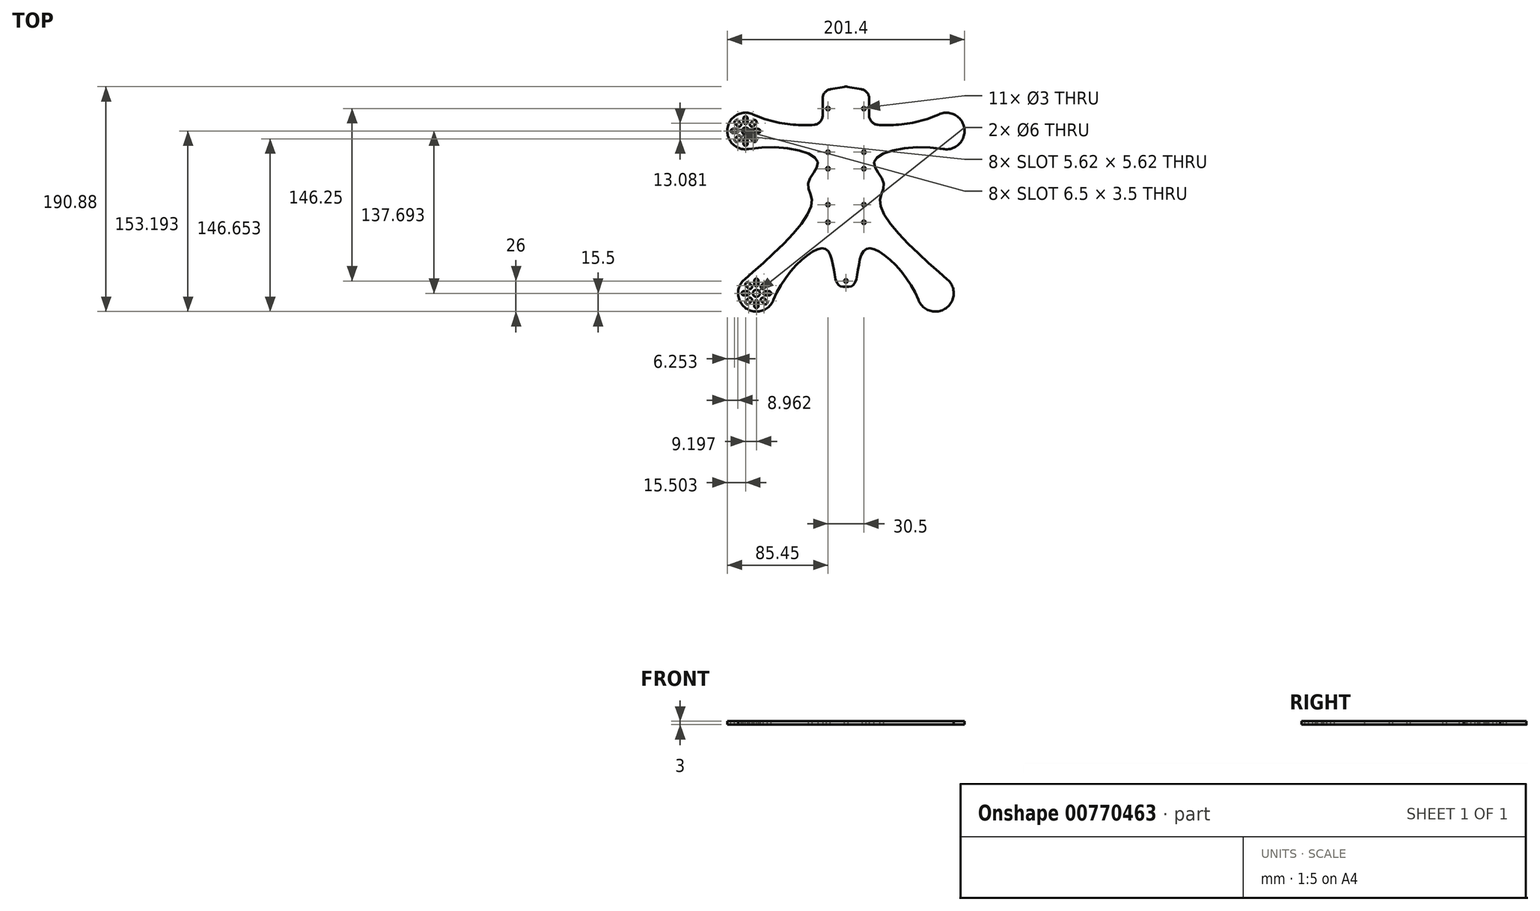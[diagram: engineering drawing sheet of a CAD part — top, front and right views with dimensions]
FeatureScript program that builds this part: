
annotation { "Feature Type Name" : "Feature", "Feature Type Description" : "" }
export const myFeature = defineFeature(function(context is Context, id is Id, definition is map)
    precondition{}
    {
        {
            var Q0;
            Q0=qCreatedBy(makeId("Top.planeOp"),FACE);
            var sketch = newSketch(context, id + "F0", { "sketchPlane" : qUnion([Q0])});
            skCircle(sketch, "E0", {"center": v(76, -77.5) * mm, "radius": 63.5 * mm, "construction": true});
            skLineSegment(sketch, "E1", {"start": v(0, 110) * mm, "end": v(0, -110) * mm, "construction": true});
            skLineSegment(sketch, "E2", {"start": v(-112.76, 0) * mm, "end": v(107.24, 0) * mm, "construction": true});
            skCircle(sketch, "E3", {"center": v(-85.2, 60.2) * mm, "radius": 63.5 * mm, "construction": true});
            skCircle(sketch, "E4", {"center": v(-76, -77.5) * mm, "radius": 63.5 * mm, "construction": true});
            skCircle(sketch, "E5", {"center": v(85.2, 60.2) * mm, "radius": 63.5 * mm, "construction": true});
            skLineSegment(sketch, "E6", {"start": v(-85.2, 60.2) * mm, "end": v(76, -77.5) * mm, "construction": true});
            skLineSegment(sketch, "E7", {"start": v(85.2, 60.2) * mm, "end": v(-76, -77.5) * mm, "construction": true});
            skLineSegment(sketch, "E8", {"start": v(-85.2, 60.2) * mm, "end": v(85.2, 60.2) * mm, "construction": true});
            skLineSegment(sketch, "E9", {"start": v(-76, -77.5) * mm, "end": v(76, -77.5) * mm, "construction": true});
            skLineSegment(sketch, "E10", {"start": v(85.2, 60.2) * mm, "end": v(76, -77.5) * mm, "construction": true});
            skLineSegment(sketch, "E11", {"start": v(-85.2, 60.2) * mm, "end": v(-76, -77.5) * mm, "construction": true});
            skCircle(sketch, "E12", {"center": v(76, -77.5) * mm, "radius": 11.5 * mm, "construction": true});
            skArc(sketch, "E13", {"start": v(61.56, -83.13) * mm, "mid": v(84.93, -90.17) * mm, "end": v(86.16, -65.8) * mm});
            skArc(sketch, "E14", {"start": v(82.42, 44.94) * mm, "mid": v(100.57, 62.2) * mm, "end": v(78.61, 74.23) * mm});
            skLineSegment(sketch, "E15", {"start": v(0, 98) * mm, "end": v(0, -72) * mm, "construction": true});
            skFitSpline(sketch, "E16", {"points": [v(82.42, 44.94) * mm, v(24, 34.2) * mm, v(32, 16.2) * mm, v(29, -2) * mm, v(86.16, -65.8) * mm], "startDerivative": vector(-245.99, 44.84) * mm, "endDerivative": vector(157.3, -136.44) * mm});
            skLineSegment(sketch, "E17", {"start": v(86.16, -65.8) * mm, "end": v(67.27, -49.4) * mm, "construction": true});
            skLineSegment(sketch, "E18", {"start": v(82.42, 44.94) * mm, "end": v(57.82, 49.43) * mm, "construction": true});
            skLineSegment(sketch, "E19.bottom", {"start": v(15.25, 28.25) * mm, "end": v(-15.25, 28.25) * mm, "construction": true});
            skLineSegment(sketch, "E19.top", {"start": v(15.25, -2.25) * mm, "end": v(-15.25, -2.25) * mm, "construction": true});
            skLineSegment(sketch, "E19.left", {"start": v(15.25, 28.25) * mm, "end": v(15.25, -2.25) * mm, "construction": true});
            skLineSegment(sketch, "E19.right", {"start": v(-15.25, 28.25) * mm, "end": v(-15.25, -2.25) * mm, "construction": true});
            skPoint(sketch, "E19.middle", {"position": v(0, 13) * mm});
            skCircle(sketch, "E20", {"center": v(15.25, 28.25) * mm, "radius": 1.5 * mm});
            skCircle(sketch, "E21", {"center": v(-15.25, 28.25) * mm, "radius": 1.5 * mm});
            skCircle(sketch, "E22", {"center": v(-15.25, -2.25) * mm, "radius": 1.5 * mm});
            skCircle(sketch, "E23", {"center": v(15.25, -2.25) * mm, "radius": 1.5 * mm});
            skLineSegment(sketch, "E24.bottom", {"start": v(18, 31) * mm, "end": v(-18, 31) * mm, "construction": true});
            skLineSegment(sketch, "E24.top", {"start": v(18, -5) * mm, "end": v(-18, -5) * mm, "construction": true});
            skLineSegment(sketch, "E24.left", {"start": v(18, 31) * mm, "end": v(18, -5) * mm, "construction": true});
            skLineSegment(sketch, "E24.right", {"start": v(-18, 31) * mm, "end": v(-18, -5) * mm, "construction": true});
            skCircle(sketch, "E25", {"center": v(15.25, 42.25) * mm, "radius": 1.5 * mm});
            skCircle(sketch, "E26", {"center": v(15.25, 79.25) * mm, "radius": 1.5 * mm});
            skCircle(sketch, "E27", {"center": v(15.25, -17.25) * mm, "radius": 1.5 * mm});
            skCircle(sketch, "E28", {"center": v(0, -67) * mm, "radius": 1.5 * mm});
            skFitSpline(sketch, "E29", {"points": [v(61.56, -83.13) * mm, v(17, -40) * mm, v(8, -68) * mm, v(0, -72) * mm], "startDerivative": vector(-56.32, 144.55) * mm, "endDerivative": vector(-62, 0) * mm});
            skLineSegment(sketch, "E30", {"start": v(0, -72) * mm, "end": v(3.8, -72) * mm});
            skLineSegment(sketch, "E31", {"start": v(61.56, -83.13) * mm, "end": v(52.48, -59.83) * mm, "construction": true});
            skFitSpline(sketch, "E32.MirrorCS", {"points": [v(-61.56, -83.13) * mm, v(-17, -40) * mm, v(-8, -68) * mm, v(0, -72) * mm], "startDerivative": vector(56.32, 144.55) * mm, "endDerivative": vector(62, 0) * mm});
            skArc(sketch, "E33.MirrorC", {"start": v(-61.56, -83.13) * mm, "mid": v(-84.93, -90.17) * mm, "end": v(-86.16, -65.8) * mm});
            skFitSpline(sketch, "E34.MirrorCS", {"points": [v(-82.42, 44.94) * mm, v(-24, 34.2) * mm, v(-32, 16.2) * mm, v(-29, -2) * mm, v(-86.16, -65.8) * mm], "startDerivative": vector(245.99, 44.84) * mm, "endDerivative": vector(-157.3, -136.44) * mm});
            skArc(sketch, "E35.MirrorC", {"start": v(-82.42, 44.94) * mm, "mid": v(-100.57, 62.2) * mm, "end": v(-78.61, 74.23) * mm});
            skLineSegment(sketch, "E36", {"start": v(15.25, -17.25) * mm, "end": v(15.25, 79.25) * mm, "construction": true});
            skCircle(sketch, "E37.MirrorC", {"center": v(-15.25, 79.25) * mm, "radius": 1.5 * mm});
            skCircle(sketch, "E38.MirrorC", {"center": v(-15.25, 42.25) * mm, "radius": 1.5 * mm});
            skCircle(sketch, "E39.MirrorC", {"center": v(-15.25, -17.25) * mm, "radius": 1.5 * mm});
            skLineSegment(sketch, "E40", {"start": v(0, 98) * mm, "end": v(19.7, 94.53) * mm});
            skLineSegment(sketch, "E41", {"start": v(19.7, 94.53) * mm, "end": v(19.7, 66.53) * mm});
            skFitSpline(sketch, "E42", {"points": [v(19.7, 66.53) * mm, v(78.61, 74.23) * mm], "startDerivative": vector(29.71, -6.37) * mm, "endDerivative": vector(67.9, 31.86) * mm});
            skLineSegment(sketch, "E43", {"start": v(78.61, 74.23) * mm, "end": v(55.98, 63.6) * mm, "construction": true});
            skLineSegment(sketch, "E44.MirrorCS", {"start": v(0, 98) * mm, "end": v(-19.7, 94.53) * mm});
            skLineSegment(sketch, "E45.MirrorCS", {"start": v(-19.7, 94.53) * mm, "end": v(-19.7, 66.53) * mm});
            skFitSpline(sketch, "E46.MirrorCS", {"points": [v(-19.7, 66.53) * mm, v(-78.61, 74.23) * mm], "startDerivative": vector(-29.71, -6.37) * mm, "endDerivative": vector(-67.9, 31.86) * mm});
            skSolve(sketch);
        }
        {
            var Q0;
            {var subQ0=sQuery(id+"F0.wireOp",EDGE,"E35.MirrorC");var subQ1=makeQuery(id+"F0.imprint","INTERSECT",VERTEX,{"derivedFrom":[sQuery(id+"F0.wireOp",EDGE,"E34.MirrorCS"),subQ0]});Q0=makeQuery(id+"F0.imprint","IMPRINT",FACE,{"disambiguationData":[TD([[makeQuery(id+"F0.imprint","IMPRINT",EDGE,{"disambiguationData":[TD([[subQ1,1.0]])],"derivedFrom":subQ0}),-1.0]])]});}
            var Q1;
            Q1=makeQuery(id+"F0.imprint","IMPRINT",FACE,{"disambiguationData":[TD([[makeQuery(id+"F0.imprint","IMPRINT",EDGE,{"derivedFrom":sQuery(id+"F0.wireOp",EDGE,"E21")}),-1.0]])]});
            var Q2;
            {var subQ6=sQuery(id+"F0.wireOp",EDGE,"eeeb82b9-f415-4523-90a6-ce32b2bf8115");Q2=makeQuery(id+"F0.imprint","IMPRINT",FACE,{"disambiguationData":[TD([[makeQuery(id+"F0.imprint","IMPRINT",EDGE,{"derivedFrom":subQ6}),1.0]])]});}
            var Q3;
            {var subQ0=sQuery(id+"F0.wireOp",EDGE,"E13");var subQ1=makeQuery(id+"F0.imprint","INTERSECT",VERTEX,{"derivedFrom":[subQ0,sQuery(id+"F0.wireOp",EDGE,"E16")]});Q3=makeQuery(id+"F0.imprint","IMPRINT",FACE,{"disambiguationData":[TD([[makeQuery(id+"F0.imprint","IMPRINT",EDGE,{"disambiguationData":[TD([[subQ1,-1.0]])],"derivedFrom":subQ0}),1.0]])]});}
            var Q4;
            {var subQ0=sQuery(id+"F0.wireOp",EDGE,"E33.MirrorC");var subQ1=makeQuery(id+"F0.imprint","INTERSECT",VERTEX,{"derivedFrom":[sQuery(id+"F0.wireOp",EDGE,"E32.MirrorCS"),subQ0]});Q4=makeQuery(id+"F0.imprint","IMPRINT",FACE,{"disambiguationData":[TD([[makeQuery(id+"F0.imprint","IMPRINT",EDGE,{"disambiguationData":[TD([[subQ1,1.0]])],"derivedFrom":subQ0}),-1.0]])]});}
            var Q5;
            {var subQ0=sQuery(id+"F0.wireOp",EDGE,"E14");var subQ1=makeQuery(id+"F0.imprint","INTERSECT",VERTEX,{"derivedFrom":[subQ0,sQuery(id+"F0.wireOp",EDGE,"eeeb82b9-f415-4523-90a6-ce32b2bf8115")]});Q5=makeQuery(id+"F0.imprint","IMPRINT",FACE,{"disambiguationData":[TD([[makeQuery(id+"F0.imprint","IMPRINT",EDGE,{"disambiguationData":[TD([[subQ1,-1.0]])],"derivedFrom":subQ0}),1.0]])]});}
            var Q6;
            {var subQ0=sQuery(id+"F0.wireOp",EDGE,"E16");Q6=makeQuery(id+"F0.imprint","IMPRINT",FACE,{"disambiguationData":[TD([[makeQuery(id+"F0.imprint","IMPRINT",EDGE,{"derivedFrom":subQ0}),-1.0]])]});}
            extrude(context, id + "F1", {"entities" : qUnion([Q0, Q1, Q2, Q3, Q4, Q5, Q6]), "depth" : 3 * mm, "offsetDistance" : 25 * mm});
        }
        {
            var Q0;
            Q0=makeQuery(id+"F1.opExtrude","SWEPT_EDGE",EDGE,{"disambiguationData":[OSD([sQuery(id+"F0.wireOp",EDGE,"E45.MirrorCS"),sQuery(id+"F0.wireOp",EDGE,"E46.MirrorCS")])]});
            var Q1;
            Q1=makeQuery(id+"F1.opExtrude","SWEPT_EDGE",EDGE,{"disambiguationData":[OSD([sQuery(id+"F0.wireOp",EDGE,"E44.MirrorCS"),sQuery(id+"F0.wireOp",EDGE,"E45.MirrorCS")])]});
            var Q2;
            Q2=makeQuery(id+"F1.opExtrude","SWEPT_EDGE",EDGE,{"disambiguationData":[OSD([sQuery(id+"F0.wireOp",EDGE,"E41"),sQuery(id+"F0.wireOp",EDGE,"E42")])]});
            var Q3;
            Q3=makeQuery(id+"F1.opExtrude","SWEPT_EDGE",EDGE,{"disambiguationData":[OSD([sQuery(id+"F0.wireOp",EDGE,"E40"),sQuery(id+"F0.wireOp",EDGE,"E41")])]});
            var Q4;
            Q4=makeQuery(id+"F1.opExtrude","SWEPT_EDGE",EDGE,{"disambiguationData":[OSD([sQuery(id+"F0.wireOp",EDGE,"E40"),sQuery(id+"F0.wireOp",EDGE,"E44.MirrorCS")])]});
            fillet(context, id + "F2", {"entities" : qUnion([Q0, Q1, Q2, Q3, Q4]), "tangentPropagation" : true, "radius" : 8 * mm, "defaultsChanged" : false, "vertexSettings" : [], "allowEdgeOverflow" : false});
        }
        {
            var Q0;
            Q0=makeQuery(id+"F1.opExtrude","CAP_FACE",FACE,{"disambiguationData":[OSD([sQuery(id+"F0.wireOp",EDGE,"E13"),sQuery(id+"F0.wireOp",EDGE,"E14"),sQuery(id+"F0.wireOp",EDGE,"E16"),sQuery(id+"F0.wireOp",EDGE,"E20"),sQuery(id+"F0.wireOp",EDGE,"E21"),sQuery(id+"F0.wireOp",EDGE,"E22"),sQuery(id+"F0.wireOp",EDGE,"E23"),sQuery(id+"F0.wireOp",EDGE,"E25"),sQuery(id+"F0.wireOp",EDGE,"E26"),sQuery(id+"F0.wireOp",EDGE,"E27"),sQuery(id+"F0.wireOp",EDGE,"E28"),sQuery(id+"F0.wireOp",EDGE,"E29"),sQuery(id+"F0.wireOp",EDGE,"E32.MirrorCS"),sQuery(id+"F0.wireOp",EDGE,"E33.MirrorC"),sQuery(id+"F0.wireOp",EDGE,"E34.MirrorCS"),sQuery(id+"F0.wireOp",EDGE,"E35.MirrorC"),sQuery(id+"F0.wireOp",EDGE,"E37.MirrorC"),sQuery(id+"F0.wireOp",EDGE,"E38.MirrorC"),sQuery(id+"F0.wireOp",EDGE,"E39.MirrorC"),sQuery(id+"F0.wireOp",EDGE,"E40"),sQuery(id+"F0.wireOp",EDGE,"E41"),sQuery(id+"F0.wireOp",EDGE,"E42"),sQuery(id+"F0.wireOp",EDGE,"E44.MirrorCS"),sQuery(id+"F0.wireOp",EDGE,"E45.MirrorCS"),sQuery(id+"F0.wireOp",EDGE,"E46.MirrorCS")])],"isStart":false});
            var sketch = newSketch(context, id + "F3", { "sketchPlane" : qUnion([Q0])});
            skArc(sketch, "E47.0", {"start": v(-82.42, 44.94) * mm, "mid": v(-100.57, 62.2) * mm, "end": v(-78.61, 74.23) * mm, "construction": true});
            skArc(sketch, "E47.1", {"start": v(82.42, 44.94) * mm, "mid": v(100.57, 62.2) * mm, "end": v(78.61, 74.23) * mm});
            skArc(sketch, "E47.2", {"start": v(61.56, -83.13) * mm, "mid": v(84.93, -90.17) * mm, "end": v(86.16, -65.8) * mm});
            skArc(sketch, "E47.3", {"start": v(-61.56, -83.13) * mm, "mid": v(-84.93, -90.17) * mm, "end": v(-86.16, -65.8) * mm, "construction": true});
            skCircle(sketch, "E48", {"center": v(-85.2, 60.2) * mm, "radius": 11.5 * mm, "construction": true});
            skCircle(sketch, "E49", {"center": v(-85.2, 60.2) * mm, "radius": 3 * mm});
            skLineSegment(sketch, "E50", {"start": v(-85.2, 70.94) * mm, "end": v(-85.2, 67.94) * mm, "construction": true});
            skArc(sketch, "E51.0.startCap", {"start": v(-86.95, 70.94) * mm, "mid": v(-85.2, 72.7) * mm, "end": v(-83.45, 70.94) * mm});
            skArc(sketch, "E51.0.endCap", {"start": v(-83.45, 67.94) * mm, "mid": v(-85.2, 66.2) * mm, "end": v(-86.95, 67.94) * mm});
            skLineSegment(sketch, "E51.0.left", {"start": v(-83.45, 70.94) * mm, "end": v(-83.45, 67.94) * mm});
            skLineSegment(sketch, "E51.0.right", {"start": v(-86.95, 70.94) * mm, "end": v(-86.95, 67.94) * mm});
            skArc(sketch, "E52.1.0", {"start": v(-94.04, 66.56) * mm, "mid": v(-94.04, 69.03) * mm, "end": v(-91.56, 69.03) * mm});
            skLineSegment(sketch, "E52.1.1", {"start": v(-91.56, 69.03) * mm, "end": v(-89.44, 66.91) * mm});
            skLineSegment(sketch, "E52.1.2", {"start": v(-94.04, 66.56) * mm, "end": v(-91.91, 64.44) * mm});
            skArc(sketch, "E52.1.3", {"start": v(-89.44, 66.91) * mm, "mid": v(-89.44, 64.44) * mm, "end": v(-91.91, 64.44) * mm});
            skArc(sketch, "E52.2.0", {"start": v(-95.95, 58.44) * mm, "mid": v(-97.7, 60.2) * mm, "end": v(-95.95, 61.94) * mm});
            skLineSegment(sketch, "E52.2.1", {"start": v(-95.95, 61.94) * mm, "end": v(-92.95, 61.94) * mm});
            skLineSegment(sketch, "E52.2.2", {"start": v(-95.95, 58.44) * mm, "end": v(-92.95, 58.44) * mm});
            skArc(sketch, "E52.2.3", {"start": v(-92.95, 61.94) * mm, "mid": v(-91.2, 60.2) * mm, "end": v(-92.95, 58.44) * mm});
            skArc(sketch, "E52.3.0", {"start": v(-91.56, 51.35) * mm, "mid": v(-94.04, 51.35) * mm, "end": v(-94.04, 53.83) * mm});
            skLineSegment(sketch, "E52.3.1", {"start": v(-94.04, 53.83) * mm, "end": v(-91.91, 55.95) * mm});
            skLineSegment(sketch, "E52.3.2", {"start": v(-91.56, 51.35) * mm, "end": v(-89.44, 53.48) * mm});
            skArc(sketch, "E52.3.3", {"start": v(-91.91, 55.95) * mm, "mid": v(-89.44, 55.95) * mm, "end": v(-89.44, 53.48) * mm});
            skArc(sketch, "E52.4.0", {"start": v(-83.45, 49.44) * mm, "mid": v(-85.2, 47.7) * mm, "end": v(-86.95, 49.44) * mm});
            skLineSegment(sketch, "E52.4.1", {"start": v(-86.95, 49.44) * mm, "end": v(-86.95, 52.44) * mm});
            skLineSegment(sketch, "E52.4.2", {"start": v(-83.45, 49.44) * mm, "end": v(-83.45, 52.44) * mm});
            skArc(sketch, "E52.4.3", {"start": v(-86.95, 52.44) * mm, "mid": v(-85.2, 54.2) * mm, "end": v(-83.45, 52.44) * mm});
            skArc(sketch, "E52.5.0", {"start": v(-76.36, 53.83) * mm, "mid": v(-76.36, 51.35) * mm, "end": v(-78.83, 51.35) * mm});
            skLineSegment(sketch, "E52.5.1", {"start": v(-78.83, 51.35) * mm, "end": v(-80.95, 53.48) * mm});
            skLineSegment(sketch, "E52.5.2", {"start": v(-76.36, 53.83) * mm, "end": v(-78.48, 55.95) * mm});
            skArc(sketch, "E52.5.3", {"start": v(-80.95, 53.48) * mm, "mid": v(-80.95, 55.95) * mm, "end": v(-78.48, 55.95) * mm});
            skArc(sketch, "E52.6.0", {"start": v(-74.45, 61.94) * mm, "mid": v(-72.7, 60.2) * mm, "end": v(-74.45, 58.44) * mm});
            skLineSegment(sketch, "E52.6.1", {"start": v(-74.45, 58.44) * mm, "end": v(-77.45, 58.44) * mm});
            skLineSegment(sketch, "E52.6.2", {"start": v(-74.45, 61.94) * mm, "end": v(-77.45, 61.94) * mm});
            skArc(sketch, "E52.6.3", {"start": v(-77.45, 58.44) * mm, "mid": v(-79.2, 60.2) * mm, "end": v(-77.45, 61.94) * mm});
            skArc(sketch, "E52.7.0", {"start": v(-78.83, 69.03) * mm, "mid": v(-76.36, 69.03) * mm, "end": v(-76.36, 66.56) * mm});
            skLineSegment(sketch, "E52.7.1", {"start": v(-76.36, 66.56) * mm, "end": v(-78.48, 64.44) * mm});
            skLineSegment(sketch, "E52.7.2", {"start": v(-78.83, 69.03) * mm, "end": v(-80.95, 66.91) * mm});
            skArc(sketch, "E52.7.3", {"start": v(-78.48, 64.44) * mm, "mid": v(-80.95, 64.44) * mm, "end": v(-80.95, 66.91) * mm});
            skCircle(sketch, "E53", {"center": v(-76, -77.5) * mm, "radius": 11.5 * mm, "construction": true});
            skCircle(sketch, "E54", {"center": v(-76, -77.5) * mm, "radius": 3 * mm});
            skLineSegment(sketch, "E55", {"start": v(-76, -66.75) * mm, "end": v(-76, -69.75) * mm, "construction": true});
            skArc(sketch, "E56.0.startCap", {"start": v(-77.75, -66.75) * mm, "mid": v(-76, -65) * mm, "end": v(-74.25, -66.75) * mm});
            skArc(sketch, "E56.0.endCap", {"start": v(-74.25, -69.75) * mm, "mid": v(-76, -71.5) * mm, "end": v(-77.75, -69.75) * mm});
            skLineSegment(sketch, "E56.0.left", {"start": v(-74.25, -66.75) * mm, "end": v(-74.25, -69.75) * mm});
            skLineSegment(sketch, "E56.0.right", {"start": v(-77.75, -66.75) * mm, "end": v(-77.75, -69.75) * mm});
            skArc(sketch, "E57.1.0", {"start": v(-84.84, -71.14) * mm, "mid": v(-84.84, -68.66) * mm, "end": v(-82.36, -68.66) * mm});
            skLineSegment(sketch, "E57.1.1", {"start": v(-82.36, -68.66) * mm, "end": v(-80.24, -70.78) * mm});
            skLineSegment(sketch, "E57.1.2", {"start": v(-84.84, -71.14) * mm, "end": v(-82.72, -73.26) * mm});
            skArc(sketch, "E57.1.3", {"start": v(-80.24, -70.78) * mm, "mid": v(-80.24, -73.26) * mm, "end": v(-82.72, -73.26) * mm});
            skArc(sketch, "E57.2.0", {"start": v(-86.75, -79.25) * mm, "mid": v(-88.5, -77.5) * mm, "end": v(-86.75, -75.75) * mm});
            skLineSegment(sketch, "E57.2.1", {"start": v(-86.75, -75.75) * mm, "end": v(-83.75, -75.75) * mm});
            skLineSegment(sketch, "E57.2.2", {"start": v(-86.75, -79.25) * mm, "end": v(-83.75, -79.25) * mm});
            skArc(sketch, "E57.2.3", {"start": v(-83.75, -75.75) * mm, "mid": v(-82, -77.5) * mm, "end": v(-83.75, -79.25) * mm});
            skArc(sketch, "E57.3.0", {"start": v(-82.36, -86.34) * mm, "mid": v(-84.84, -86.34) * mm, "end": v(-84.84, -83.86) * mm});
            skLineSegment(sketch, "E57.3.1", {"start": v(-84.84, -83.86) * mm, "end": v(-82.72, -81.74) * mm});
            skLineSegment(sketch, "E57.3.2", {"start": v(-82.36, -86.34) * mm, "end": v(-80.24, -84.22) * mm});
            skArc(sketch, "E57.3.3", {"start": v(-82.72, -81.74) * mm, "mid": v(-80.24, -81.74) * mm, "end": v(-80.24, -84.22) * mm});
            skArc(sketch, "E57.4.0", {"start": v(-74.25, -88.25) * mm, "mid": v(-76, -90) * mm, "end": v(-77.75, -88.25) * mm});
            skLineSegment(sketch, "E57.4.1", {"start": v(-77.75, -88.25) * mm, "end": v(-77.75, -85.25) * mm});
            skLineSegment(sketch, "E57.4.2", {"start": v(-74.25, -88.25) * mm, "end": v(-74.25, -85.25) * mm});
            skArc(sketch, "E57.4.3", {"start": v(-77.75, -85.25) * mm, "mid": v(-76, -83.5) * mm, "end": v(-74.25, -85.25) * mm});
            skArc(sketch, "E57.5.0", {"start": v(-67.16, -83.86) * mm, "mid": v(-67.16, -86.34) * mm, "end": v(-69.64, -86.34) * mm});
            skLineSegment(sketch, "E57.5.1", {"start": v(-69.64, -86.34) * mm, "end": v(-71.76, -84.22) * mm});
            skLineSegment(sketch, "E57.5.2", {"start": v(-67.16, -83.86) * mm, "end": v(-69.28, -81.74) * mm});
            skArc(sketch, "E57.5.3", {"start": v(-71.76, -84.22) * mm, "mid": v(-71.76, -81.74) * mm, "end": v(-69.28, -81.74) * mm});
            skArc(sketch, "E57.6.0", {"start": v(-65.25, -75.75) * mm, "mid": v(-63.5, -77.5) * mm, "end": v(-65.25, -79.25) * mm});
            skLineSegment(sketch, "E57.6.1", {"start": v(-65.25, -79.25) * mm, "end": v(-68.25, -79.25) * mm});
            skLineSegment(sketch, "E57.6.2", {"start": v(-65.25, -75.75) * mm, "end": v(-68.25, -75.75) * mm});
            skArc(sketch, "E57.6.3", {"start": v(-68.25, -79.25) * mm, "mid": v(-70, -77.5) * mm, "end": v(-68.25, -75.75) * mm});
            skArc(sketch, "E57.7.0", {"start": v(-69.64, -68.66) * mm, "mid": v(-67.16, -68.66) * mm, "end": v(-67.16, -71.14) * mm});
            skLineSegment(sketch, "E57.7.1", {"start": v(-67.16, -71.14) * mm, "end": v(-69.28, -73.26) * mm});
            skLineSegment(sketch, "E57.7.2", {"start": v(-69.64, -68.66) * mm, "end": v(-71.76, -70.78) * mm});
            skArc(sketch, "E57.7.3", {"start": v(-69.28, -73.26) * mm, "mid": v(-71.76, -73.26) * mm, "end": v(-71.76, -70.78) * mm});
            skSolve(sketch);
        }
        {
            var Q0;
            Q0 = qSketchRegion(id + "F3", true);
            extrude(context, id + "F4", {"entities" : qUnion([Q0]), "operationType" : NewBodyOperationType.REMOVE, "oppositeDirection" : true, "depth" : 25 * mm, "offsetDistance" : 25 * mm});
        }
        {
            var Q0;
            Q0=makeQuery(id+"F1.opExtrude","CAP_FACE",FACE,{"disambiguationData":[OSD([sQuery(id+"F0.wireOp",EDGE,"E13"),sQuery(id+"F0.wireOp",EDGE,"E14"),sQuery(id+"F0.wireOp",EDGE,"E16"),sQuery(id+"F0.wireOp",EDGE,"E20"),sQuery(id+"F0.wireOp",EDGE,"E21"),sQuery(id+"F0.wireOp",EDGE,"E22"),sQuery(id+"F0.wireOp",EDGE,"E23"),sQuery(id+"F0.wireOp",EDGE,"E25"),sQuery(id+"F0.wireOp",EDGE,"E26"),sQuery(id+"F0.wireOp",EDGE,"E27"),sQuery(id+"F0.wireOp",EDGE,"E28"),sQuery(id+"F0.wireOp",EDGE,"E29"),sQuery(id+"F0.wireOp",EDGE,"E32.MirrorCS"),sQuery(id+"F0.wireOp",EDGE,"E33.MirrorC"),sQuery(id+"F0.wireOp",EDGE,"E34.MirrorCS"),sQuery(id+"F0.wireOp",EDGE,"E35.MirrorC"),sQuery(id+"F0.wireOp",EDGE,"E37.MirrorC"),sQuery(id+"F0.wireOp",EDGE,"E38.MirrorC"),sQuery(id+"F0.wireOp",EDGE,"E39.MirrorC"),sQuery(id+"F0.wireOp",EDGE,"E40"),sQuery(id+"F0.wireOp",EDGE,"E41"),sQuery(id+"F0.wireOp",EDGE,"E42"),sQuery(id+"F0.wireOp",EDGE,"E44.MirrorCS"),sQuery(id+"F0.wireOp",EDGE,"E45.MirrorCS"),sQuery(id+"F0.wireOp",EDGE,"E46.MirrorCS")])],"isStart":false});
            cPlane(context, id + "F5", {"entities" : qUnion([Q0]), "cplaneType" : CPlaneType.OFFSET, "offset" : 30 * mm, "width" : 150 * mm, "height" : 150 * mm});
        }
    });
